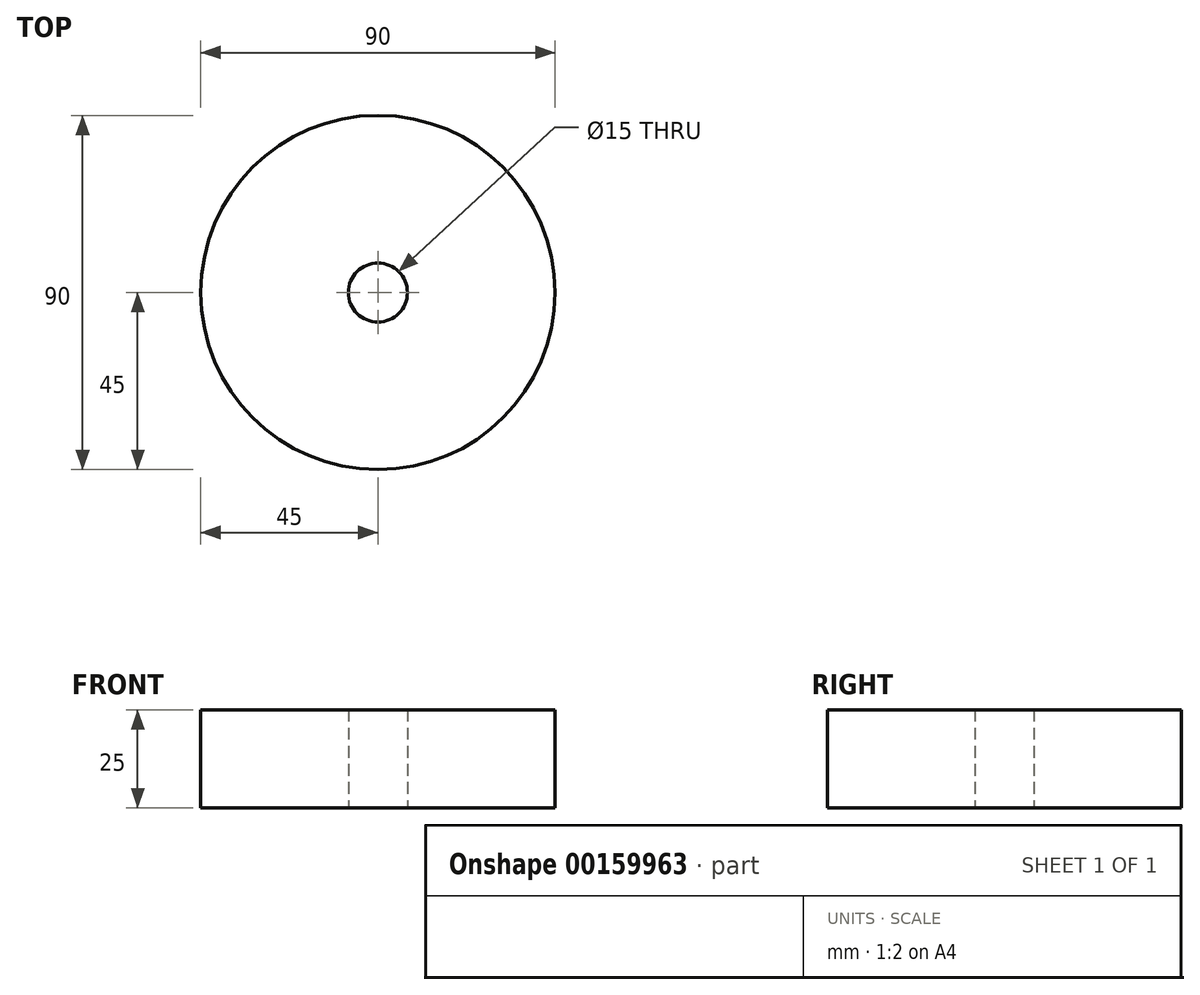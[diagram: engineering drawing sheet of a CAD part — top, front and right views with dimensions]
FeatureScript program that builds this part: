
annotation { "Feature Type Name" : "Feature", "Feature Type Description" : "" }
export const myFeature = defineFeature(function(context is Context, id is Id, definition is map)
    precondition{}
    {
        {
            var Q0;
            Q0=qCreatedBy(makeId("Top.planeOp"),FACE);
            var sketch = newSketch(context, id + "F0", { "sketchPlane" : qUnion([Q0])});
            skCircle(sketch, "E0", {"center": v(0, 0) * mm, "radius": 45 * mm});
            skCircle(sketch, "E1", {"center": v(0, 0) * mm, "radius": 7.5 * mm});
            skSolve(sketch);
        }
        {
            var Q0;
            Q0=makeQuery(id+"F0.imprint","IMPRINT",FACE,{"disambiguationData":[TD([[makeQuery(id+"F0.imprint","IMPRINT",EDGE,{"derivedFrom":sQuery(id+"F0.wireOp",EDGE,"E0")}),1.0]])]});
            extrude(context, id + "F1", {"entities" : qUnion([Q0]), "depth" : 25 * mm});
        }
    });
